# Revit family: Sunshade-Linear-Kawneer-Storefront-Curved
name_source: partatom
category: Specialty Equipment
revit_build: Autodesk Revit 2015 (Build: 20140905_0730(x64)
units: mm (PartAtom-declared; Revit-internal decimal feet)

## types (3) — shared parameters
Blade Count = 5
Blades Distance = 0' - 4 1/2"
Bottom Inset Distance = 0' - 5"
CTRL Length = 2' - 6"
Default Elevation = 4' - 0"
Description = Square Outrigger, Rectangle Fascias
Distance Blade 1 and 2 = 0' - 0 1/8"
Distance Blade 2 and 3 = 0' - 0 7/16"
Distance Blade 3 and 4 = 0' - 0 11/16"
Distance Blade 4 and 5 = 0' - 0 15/16"
Distance Blade 5 and 6 = 0' - 0 7/8"
Finish = Aluminum - Kawneer - Clear
Has 6th Blade = No
Length = 2' - 6"
Manufacturer = Kawneer
Model = Sunshade Linear Storefront
Product Documentation Link = http://www.kawneer.com
Product Page URL = http://www.kawneer.com
Product data url = https://bimobject.com
URL = http://www.kawneer.com

## per-type parameters (varying)
| type | Blade Type |
| 30"-Circular | Blade-Kawneer-Circular : Versoleil |
| 30"-Diamond | Blade-Kawneer-Diamond : Versoleil |
| 30"-Square | Blade-Kawneer-Square : Versoleil |

## geometry (parser evidence)
native form markers: Sweep x13
no freeform markers — native parametric forms only
